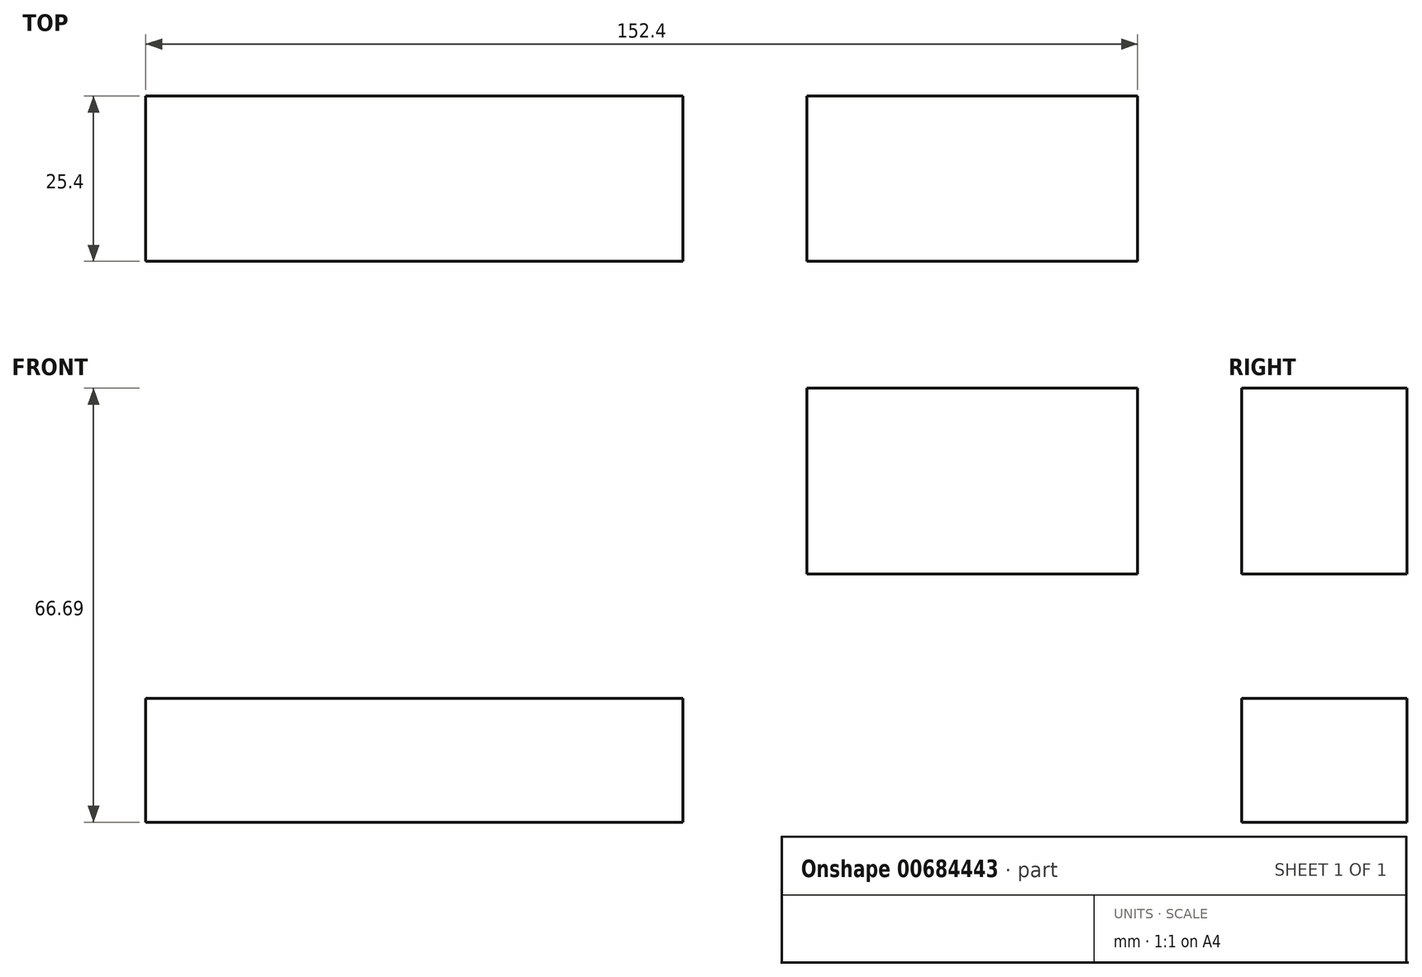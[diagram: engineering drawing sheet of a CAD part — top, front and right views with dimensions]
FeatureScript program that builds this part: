
annotation { "Feature Type Name" : "Feature", "Feature Type Description" : "" }
export const myFeature = defineFeature(function(context is Context, id is Id, definition is map)
    precondition{}
    {
        {
            var Q0;
            Q0=qCreatedBy(makeId("Front.planeOp"),FACE);
            var sketch = newSketch(context, id + "F0", { "sketchPlane" : qUnion([Q0])});
            skLineSegment(sketch, "E0.bottom", {"start": v(-41.28, -9.52) * mm, "end": v(41.28, -9.52) * mm});
            skLineSegment(sketch, "E0.top", {"start": v(-41.28, 9.53) * mm, "end": v(41.27, 9.53) * mm});
            skLineSegment(sketch, "E0.left", {"start": v(-41.27, -9.52) * mm, "end": v(-41.28, 9.53) * mm});
            skLineSegment(sketch, "E0.right", {"start": v(41.28, -9.52) * mm, "end": v(41.28, 9.53) * mm});
            skPoint(sketch, "E0.middle", {"position": v(0, 0) * mm});
            skLineSegment(sketch, "E1.bottom", {"start": v(60.33, 28.59) * mm, "end": v(111.13, 28.59) * mm});
            skLineSegment(sketch, "E1.top", {"start": v(60.33, 57.16) * mm, "end": v(111.13, 57.16) * mm});
            skLineSegment(sketch, "E1.left", {"start": v(60.33, 28.59) * mm, "end": v(60.33, 57.16) * mm});
            skLineSegment(sketch, "E1.right", {"start": v(111.12, 28.59) * mm, "end": v(111.12, 57.16) * mm});
            skPoint(sketch, "E1.middle", {"position": v(85.72, 42.88) * mm});
            skLineSegment(sketch, "E2", {"start": v(41.28, 9.53) * mm, "end": v(41.28, 27) * mm});
            skArc(sketch, "E3", {"start": v(41.28, 27) * mm, "mid": v(45.92, 38.23) * mm, "end": v(57.15, 42.88) * mm});
            skLineSegment(sketch, "E4", {"start": v(57.15, 42.88) * mm, "end": v(72.96, 42.88) * mm});
            skPoint(sketch, "E4.endSnap0", {"position": v(60.33, 42.88) * mm});
            skArc(sketch, "E5.0", {"start": v(22.23, 27) * mm, "mid": v(32.45, 51.7) * mm, "end": v(57.15, 61.93) * mm});
            skLineSegment(sketch, "E5.1", {"start": v(22.23, -7.82) * mm, "end": v(22.23, 27) * mm});
            skSolve(sketch);
        }
        {
            var Q0;
            Q0 = qSketchRegion(id + "F0", true);
            extrude(context, id + "F1", {"entities" : qUnion([Q0]), "depth" : 25.4 * mm, "offsetDistance" : 25.4 * mm});
        }
    });
